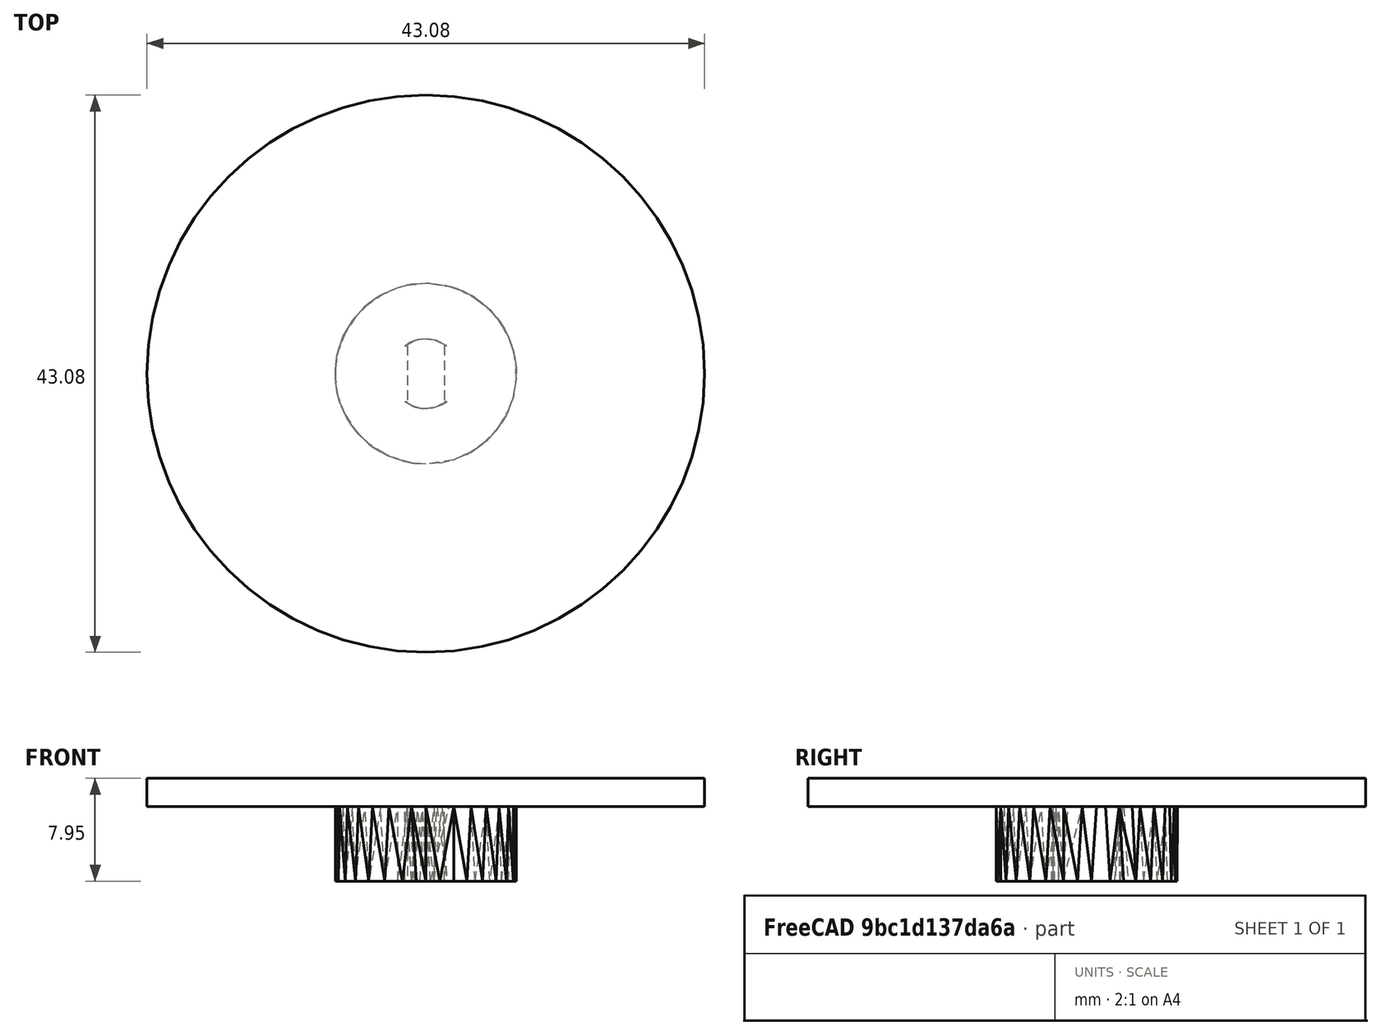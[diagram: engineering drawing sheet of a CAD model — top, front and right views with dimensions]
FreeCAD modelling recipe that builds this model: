
FCSTD DOCUMENT  (FreeCAD 0.19R24267 +148 (Git))
Label: FED disc base
License: All rights reserved
LicenseURL: http://en.wikipedia.org/wiki/All_rights_reserved
objects: Part::Feature×1, PartDesign::FeatureBase×1, Sketcher::SketchObject×1, PartDesign::Body×1, Part::Extrusion×1, Part::MultiFuse×1
note: 6 computed .brp shape members not serialized (recipe doc carries the construction recipe); baked Part::Feature solids carry a one-line shape summary decoded from their .brp

FEATURE [Part::Feature] Body001001
  shape: bbox 13.96 x 14 x 5.751 mm, 148 faces (baked)
FEATURE [PartDesign::FeatureBase] BaseFeature003
  BaseFeature = -> Body001001
FEATURE [Sketcher::SketchObject] Sketch
  FullyConstrained = false
  MapMode = 5
  Placement = pos=(0,0,8.001) rot=(0,0,1;0rad)
  Support = -> [BaseFeature003]
  sketch-geometry (1):
    g0: Circle CenterX=0 CenterY=0 CenterZ=0 NormalX=0 NormalY=0 NormalZ=1 AngleXU=0 Radius=21.5397
  constraints (1):
    c: Coincident(g0,g-1)
FEATURE [PartDesign::Body] Body001002
  BaseFeature = -> Body001001
  Group = -> [BaseFeature003,Sketch]
  Origin = -> Origin003
  Tip = -> BaseFeature003
FEATURE [Part::Extrusion] Extrude
  Base = -> Sketch
  Dir = (0,0,1)
  DirMode = 2
  FaceMakerClass = Part::FaceMakerBullseye
  LengthFwd = 2.2
  LengthRev = 0
  Solid = true
  Symmetric = false
FEATURE [Part::MultiFuse] Fusion
  Shapes = -> [Body001002,Extrude]
